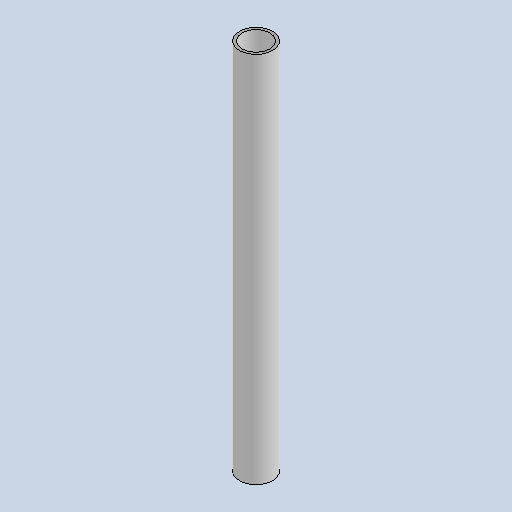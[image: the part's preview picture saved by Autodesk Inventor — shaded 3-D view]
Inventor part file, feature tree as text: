
AUTODESK INVENTOR PART (.ipt)
format: ipt  version: 2025 (Build 290162010, 162A)  size: 138,240 bytes
history: native  units: mm
features: extrude x1, sketch x1
ambient origin geometry x8: Origin, YZ Plane, XZ Plane, XY Plane, X Axis, Y Axis, Z Axis, Center Point
bodies: Solid1 (feature_tree)
feature tree (2):
  extrude  "Extrusion1"  Depth=1400.0mm
  sketch  "Sketch1"  dims[d0=125.0mm d1=104.0mm d2=1400.0mm d3=0.0mm]
